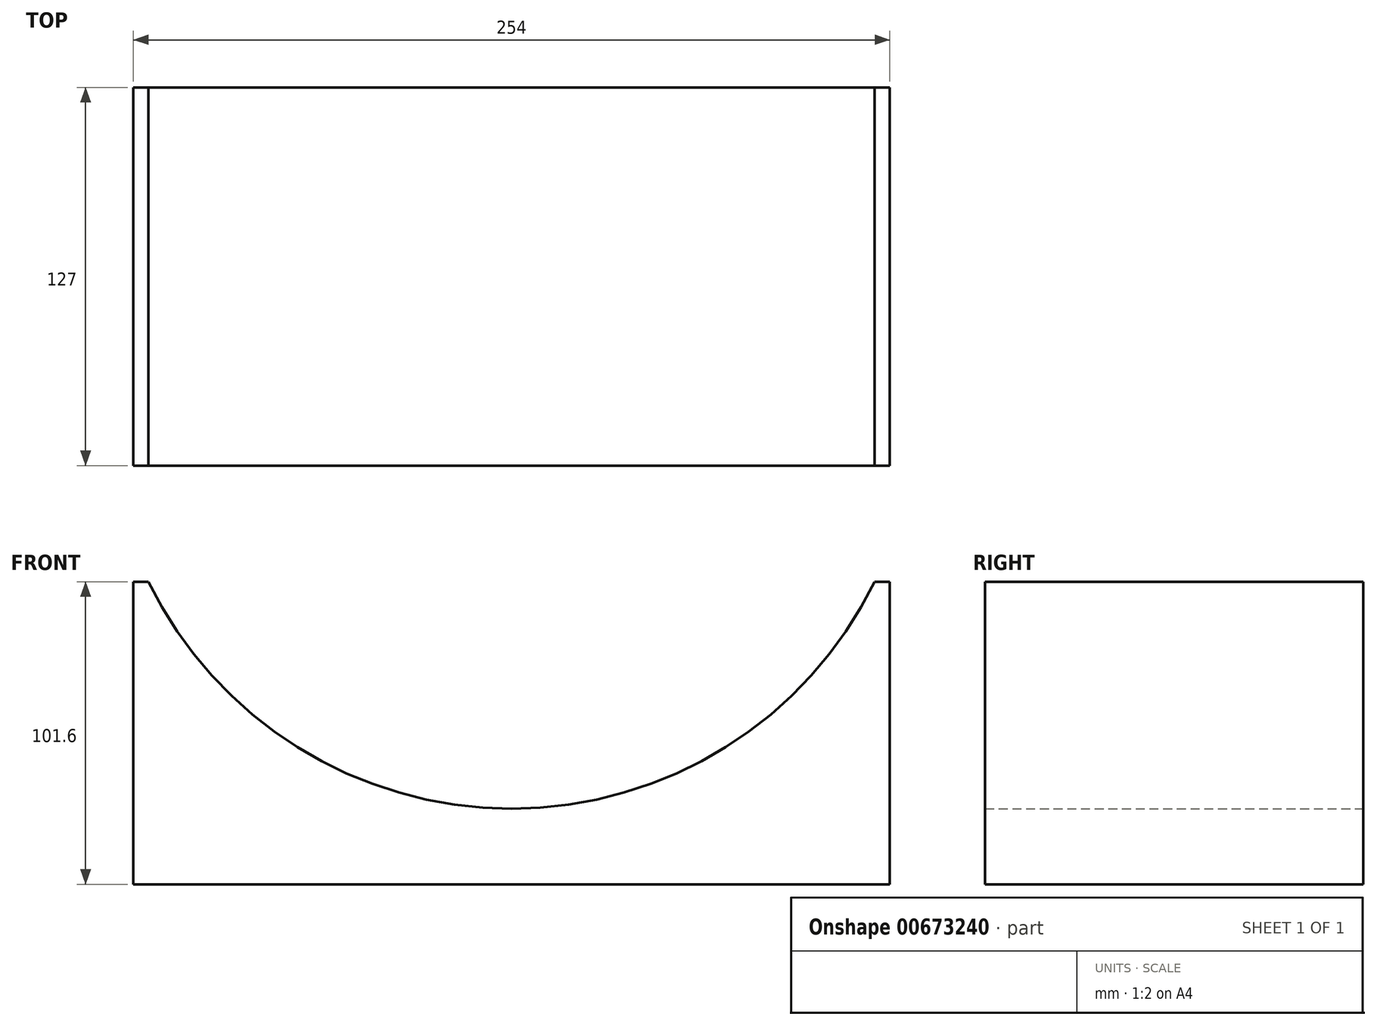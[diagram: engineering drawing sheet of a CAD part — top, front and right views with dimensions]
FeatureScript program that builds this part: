
annotation { "Feature Type Name" : "Feature", "Feature Type Description" : "" }
export const myFeature = defineFeature(function(context is Context, id is Id, definition is map)
    precondition{}
    {
        {
            var Q0;
            Q0=qCreatedBy(makeId("Front.planeOp"),FACE);
            var sketch = newSketch(context, id + "F0", { "sketchPlane" : qUnion([Q0])});
            skLineSegment(sketch, "E0", {"start": v(-126.74, 0) * mm, "end": v(127.26, 0) * mm});
            skLineSegment(sketch, "E1", {"start": v(-126.74, 0) * mm, "end": v(-126.74, 101.6) * mm});
            skLineSegment(sketch, "E2", {"start": v(-126.74, 101.6) * mm, "end": v(-121.66, 101.6) * mm});
            skLineSegment(sketch, "E3", {"start": v(127.26, 0) * mm, "end": v(127.26, 101.6) * mm});
            skLineSegment(sketch, "E4", {"start": v(127.26, 101.6) * mm, "end": v(122.18, 101.6) * mm});
            skLineSegment(sketch, "E5", {"start": v(0, 0) * mm, "end": v(0, 135.47) * mm, "construction": true});
            skArc(sketch, "E6", {"start": v(-121.66, 101.6) * mm, "mid": v(0.26, 25.4) * mm, "end": v(122.18, 101.6) * mm});
            skLineSegment(sketch, "E7", {"start": v(0.26, 25.4) * mm, "end": v(0, 0) * mm});
            skSolve(sketch);
        }
        {
            var Q0;
            Q0 = qSketchRegion(id + "F0", true);
            extrude(context, id + "F1", {"entities" : qUnion([Q0]), "endBound" : BoundingType.SYMMETRIC, "depth" : 127 * mm, "offsetDistance" : 25.4 * mm});
        }
    });
